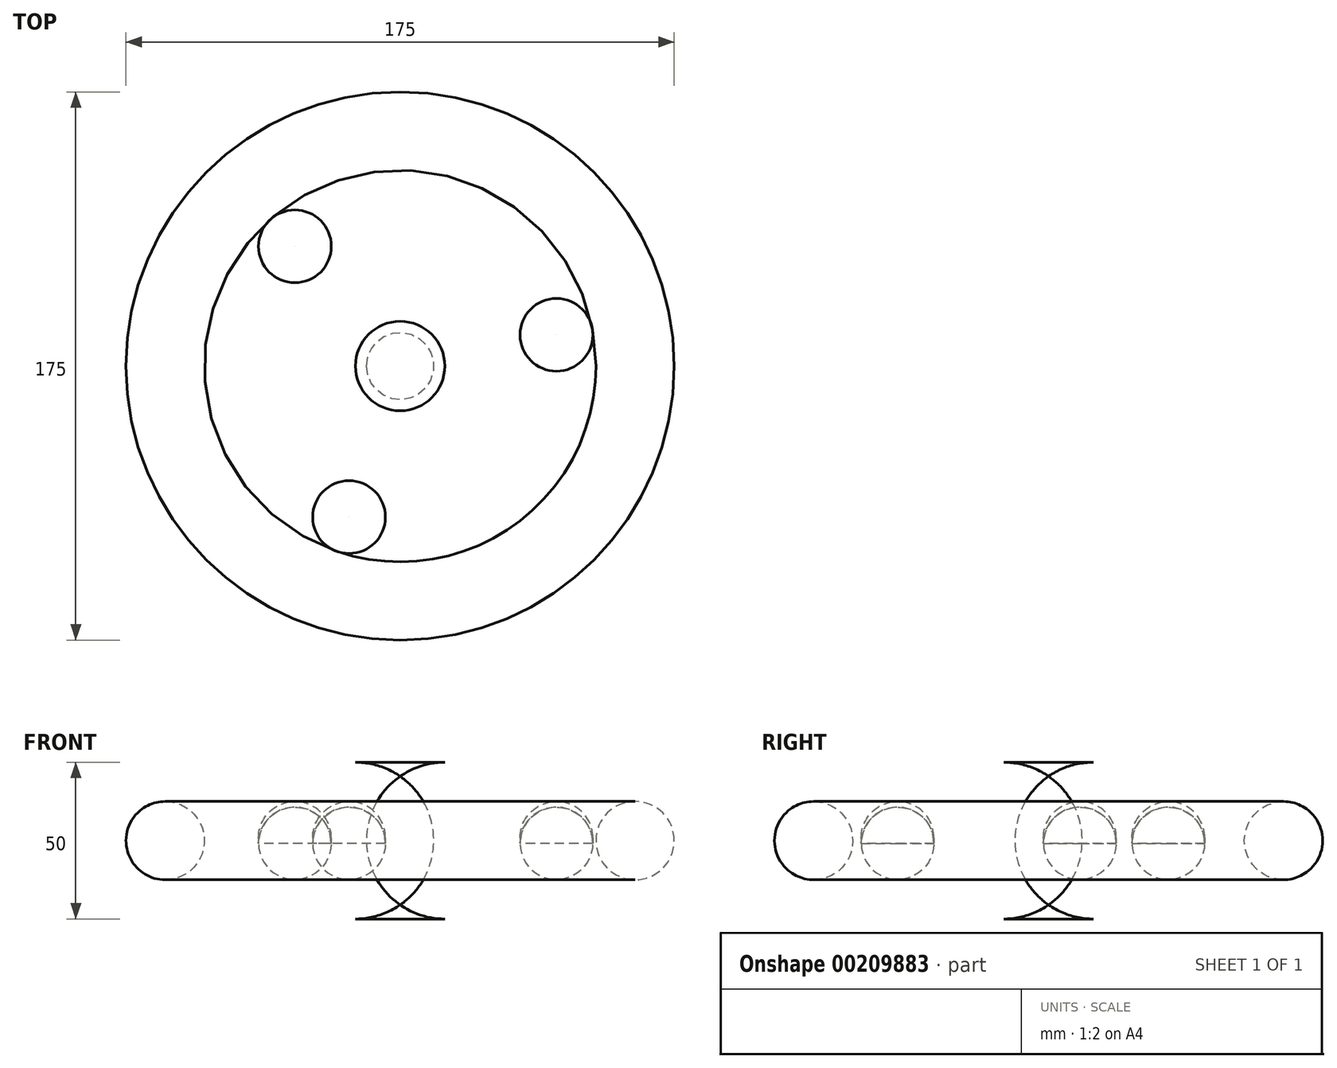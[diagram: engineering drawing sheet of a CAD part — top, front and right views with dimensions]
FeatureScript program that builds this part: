
annotation { "Feature Type Name" : "Feature", "Feature Type Description" : "" }
export const myFeature = defineFeature(function(context is Context, id is Id, definition is map)
    precondition{}
    {
        {
            var Q0;
            Q0=qCreatedBy(makeId("Top.planeOp"),FACE);
            var sketch = newSketch(context, id + "F0", { "sketchPlane" : qUnion([Q0])});
            skCircle(sketch, "E0", {"center": v(0, 0) * mm, "radius": 62.5 * mm});
            skCircle(sketch, "E1", {"center": v(0, 0) * mm, "radius": 87.5 * mm});
            skCircle(sketch, "E2.cCircle", {"center": v(0, 0) * mm, "radius": 62.5 * mm, "construction": true});
            skLineSegment(sketch, "E3.0", {"start": v(49.9, 9.98) * mm, "end": v(-16.3, -48.2) * mm, "construction": true});
            skLineSegment(sketch, "E3.1", {"start": v(-16.3, -48.2) * mm, "end": v(-33.6, 38.22) * mm, "construction": true});
            skLineSegment(sketch, "E3.2", {"start": v(-33.6, 38.22) * mm, "end": v(49.9, 9.98) * mm, "construction": true});
            skCircle(sketch, "E4", {"center": v(-33.6, 38.22) * mm, "radius": 11.62 * mm});
            skCircle(sketch, "E5", {"center": v(-16.3, -48.2) * mm, "radius": 11.62 * mm});
            skCircle(sketch, "E6", {"center": v(49.9, 9.98) * mm, "radius": 11.62 * mm});
            skCircle(sketch, "E7", {"center": v(0, 0) * mm, "radius": 39.27 * mm});
            skSolve(sketch);
        }
        {
            var Q0;
            Q0=makeQuery(id+"F0.imprint","IMPRINT",FACE,{"disambiguationData":[TD([[makeQuery(id+"F0.imprint","IMPRINT",EDGE,{"derivedFrom":sQuery(id+"F0.wireOp",EDGE,"E0")}),-1.0]])]});
            extrude(context, id + "F1", {"entities" : qUnion([Q0]), "endBound" : BoundingType.SYMMETRIC, "depth" : 25 * mm});
        }
        {
            var Q0;
            Q0=makeQuery(id+"F1.opExtrude","CAP_FACE",FACE,{"disambiguationData":[OSD([sQuery(id+"F0.wireOp",EDGE,"E0"),sQuery(id+"F0.wireOp",EDGE,"E1")])],"isStart":false});
            var Q1;
            Q1=makeQuery(id+"F1.opExtrude","CAP_FACE",FACE,{"disambiguationData":[OSD([sQuery(id+"F0.wireOp",EDGE,"E0"),sQuery(id+"F0.wireOp",EDGE,"E1")])],"isStart":true});
            fillet(context, id + "F2", {"entities" : qUnion([Q0, Q1]), "radius" : 12.5 * mm, "tangentPropagation" : true, "allowEdgeOverflow" : false});
        }
        {
            var Q0;
            {var subQ0=sQuery(id+"F0.wireOp",EDGE,"E4");var subQ1=makeQuery(id+"F0.imprint","INTERSECT",VERTEX,{"derivedFrom":[sQuery(id+"F0.wireOp",EDGE,"E0"),subQ0]});Q0=makeQuery(id+"F0.imprint","IMPRINT",FACE,{"disambiguationData":[TD([[makeQuery(id+"F0.imprint","IMPRINT",EDGE,{"disambiguationData":[TD([[subQ1,-1.0]])],"derivedFrom":subQ0}),1.0]])]});}
            var Q1;
            {var subQ0=sQuery(id+"F0.wireOp",EDGE,"E6");var subQ1=makeQuery(id+"F0.imprint","INTERSECT",VERTEX,{"derivedFrom":[sQuery(id+"F0.wireOp",EDGE,"E0"),subQ0]});Q1=makeQuery(id+"F0.imprint","IMPRINT",FACE,{"disambiguationData":[TD([[makeQuery(id+"F0.imprint","IMPRINT",EDGE,{"disambiguationData":[TD([[subQ1,-1.0]])],"derivedFrom":subQ0}),1.0]])]});}
            var Q2;
            {var subQ0=sQuery(id+"F0.wireOp",EDGE,"E5");var subQ1=makeQuery(id+"F0.imprint","INTERSECT",VERTEX,{"derivedFrom":[sQuery(id+"F0.wireOp",EDGE,"E0"),subQ0]});Q2=makeQuery(id+"F0.imprint","IMPRINT",FACE,{"disambiguationData":[TD([[makeQuery(id+"F0.imprint","IMPRINT",EDGE,{"disambiguationData":[TD([[subQ1,1.0]])],"derivedFrom":subQ0}),1.0]])]});}
            extrude(context, id + "F3", {"entities" : qUnion([Q0, Q1, Q2]), "endBound" : BoundingType.SYMMETRIC, "depth" : 25 * mm});
        }
        {
            var Q0;
            Q0=makeQuery(id+"F3.opExtrude","CAP_FACE",FACE,{"disambiguationData":[OSD([sQuery(id+"F0.wireOp",EDGE,"E4")])],"isStart":false});
            var Q1;
            Q1=makeQuery(id+"F3.opExtrude","CAP_FACE",FACE,{"disambiguationData":[OSD([sQuery(id+"F0.wireOp",EDGE,"E6")])],"isStart":false});
            var Q2;
            Q2=makeQuery(id+"F3.opExtrude","CAP_FACE",FACE,{"disambiguationData":[OSD([sQuery(id+"F0.wireOp",EDGE,"E5")])],"isStart":false});
            var Q3;
            Q3=makeQuery(id+"F3.opExtrude","CAP_FACE",FACE,{"disambiguationData":[OSD([sQuery(id+"F0.wireOp",EDGE,"E4")])],"isStart":true});
            var Q4;
            Q4=makeQuery(id+"F3.opExtrude","CAP_FACE",FACE,{"disambiguationData":[OSD([sQuery(id+"F0.wireOp",EDGE,"E6")])],"isStart":true});
            var Q5;
            Q5=makeQuery(id+"F3.opExtrude","CAP_FACE",FACE,{"disambiguationData":[OSD([sQuery(id+"F0.wireOp",EDGE,"E5")])],"isStart":true});
            fillet(context, id + "F4", {"entities" : qUnion([Q0, Q1, Q2, Q3, Q4, Q5]), "radius" : 11.6 * mm, "tangentPropagation" : true, "allowEdgeOverflow" : false});
        }
        {
            var Q0;
            {var subQ0=sQuery(id+"F0.wireOp",EDGE,"E7");var subQ1=makeQuery(id+"F0.imprint","INTERSECT",VERTEX,{"derivedFrom":[sQuery(id+"F0.wireOp",EDGE,"E4"),subQ0]});Q0=makeQuery(id+"F0.imprint","IMPRINT",FACE,{"disambiguationData":[TD([[makeQuery(id+"F0.imprint","IMPRINT",EDGE,{"disambiguationData":[TD([[subQ1,1.0]])],"derivedFrom":subQ0}),1.0]])]});}
            extrude(context, id + "F5", {"entities" : qUnion([Q0]), "endBound" : BoundingType.SYMMETRIC, "depth" : 50 * mm});
        }
        {
            var Q0;
            Q0=makeQuery(id+"F5.opExtrude","CAP_FACE",FACE,{"disambiguationData":[OSD([sQuery(id+"F0.wireOp",EDGE,"E7")])],"isStart":false});
            var Q1;
            Q1=makeQuery(id+"F5.opExtrude","CAP_FACE",FACE,{"disambiguationData":[OSD([sQuery(id+"F0.wireOp",EDGE,"E7")])],"isStart":true});
            fillet(context, id + "F6", {"entities" : qUnion([Q0, Q1]), "radius" : 25 * mm, "tangentPropagation" : true, "allowEdgeOverflow" : false});
        }
    });
